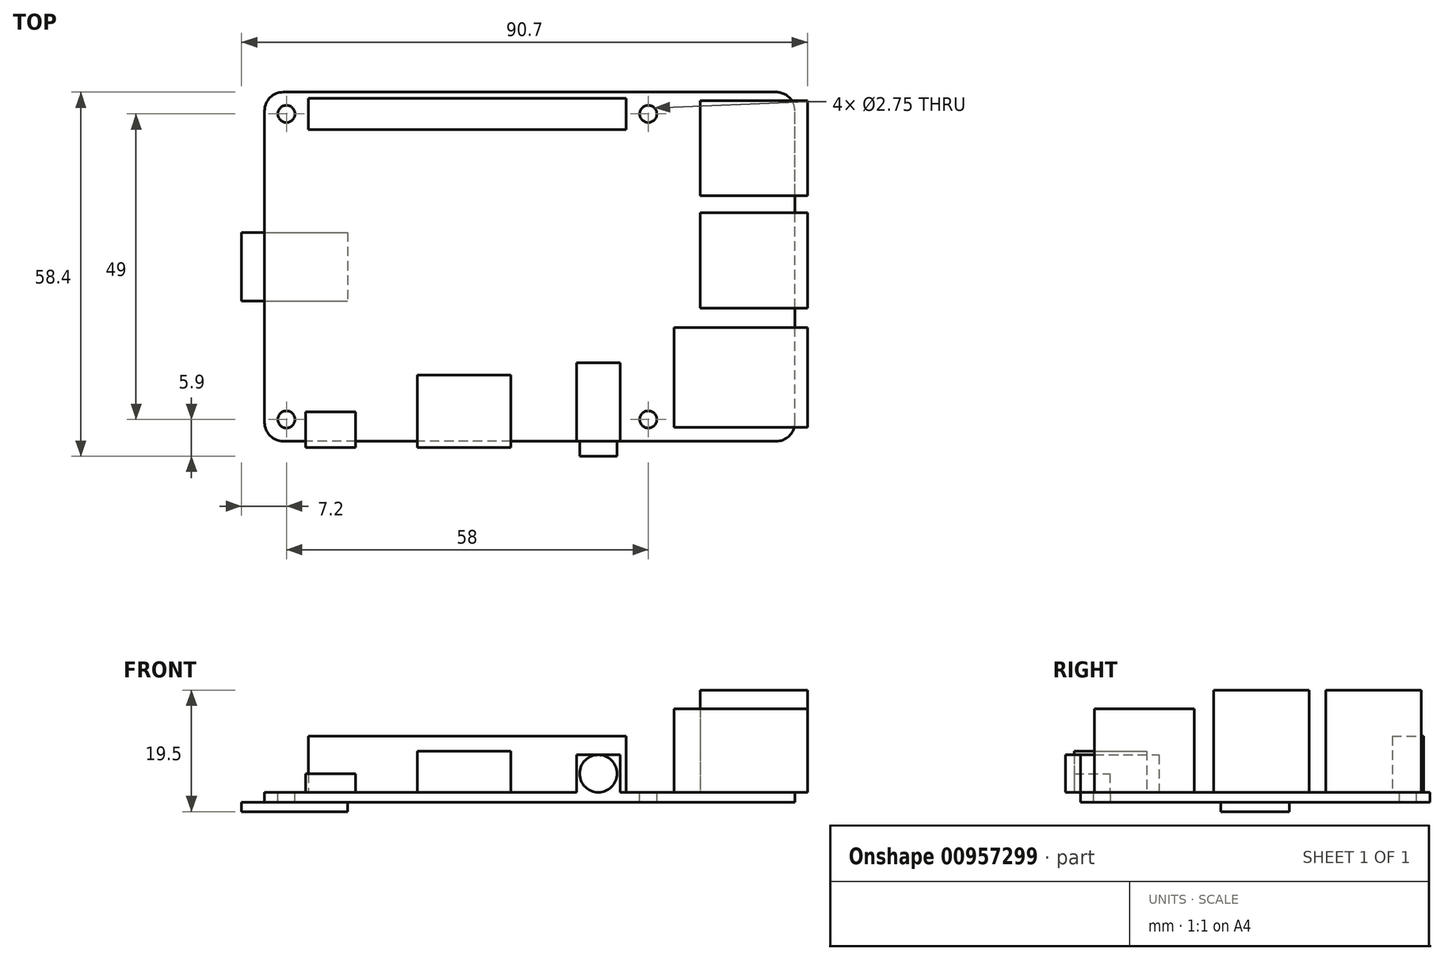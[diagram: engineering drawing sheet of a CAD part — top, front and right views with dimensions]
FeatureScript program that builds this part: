
annotation { "Feature Type Name" : "Feature", "Feature Type Description" : "" }
export const myFeature = defineFeature(function(context is Context, id is Id, definition is map)
    precondition{}
    {
        {
            var Q0;
            Q0=qCreatedBy(makeId("Top.planeOp"),FACE);
            var sketch = newSketch(context, id + "F0", { "sketchPlane" : qUnion([Q0])});
            skLineSegment(sketch, "E0.bottom", {"start": v(42.5, -28) * mm, "end": v(-42.5, -28) * mm});
            skLineSegment(sketch, "E0.top", {"start": v(42.5, 28) * mm, "end": v(-42.5, 28) * mm});
            skLineSegment(sketch, "E0.left", {"start": v(42.5, -28) * mm, "end": v(42.5, 28) * mm});
            skLineSegment(sketch, "E0.right", {"start": v(-42.5, -28) * mm, "end": v(-42.5, 28) * mm});
            skPoint(sketch, "E0.middle", {"position": v(0, 0) * mm});
            skSolve(sketch);
        }
        {
            var Q0;
            Q0=qSketchRegion(id+"F0",true);
            extrude(context, id + "F1", {"entities" : qUnion([Q0]), "depth" : 1.6 * mm, "offsetDistance" : 25 * mm});
        }
        {
            var Q0;
            Q0=makeQuery(id+"F1.opExtrude","CAP_FACE",FACE,{"disambiguationData":[OSD([sQuery(id+"F0.wireOp",EDGE,"E0.bottom"),sQuery(id+"F0.wireOp",EDGE,"E0.top"),sQuery(id+"F0.wireOp",EDGE,"E0.left"),sQuery(id+"F0.wireOp",EDGE,"E0.right")])],"isStart":false});
            var sketch = newSketch(context, id + "F2", { "sketchPlane" : qUnion([Q0])});
            skLineSegment(sketch, "E1.bottom", {"start": v(44.5, -25.75) * mm, "end": v(23.1, -25.75) * mm});
            skLineSegment(sketch, "E1.top", {"start": v(44.5, -9.75) * mm, "end": v(23.1, -9.75) * mm});
            skLineSegment(sketch, "E1.left", {"start": v(44.5, -25.75) * mm, "end": v(44.5, -9.75) * mm});
            skLineSegment(sketch, "E1.right", {"start": v(23.1, -25.75) * mm, "end": v(23.1, -9.75) * mm});
            skPoint(sketch, "E1.middle", {"position": v(33.8, -17.75) * mm});
            skSolve(sketch);
        }
        {
            var Q0;
            Q0=qSketchRegion(id+"F2",true);
            extrude(context, id + "F3", {"entities" : qUnion([Q0]), "operationType" : NewBodyOperationType.ADD, "depth" : 13.4 * mm, "offsetDistance" : 25 * mm});
        }
        {
            var Q0;
            Q0=makeQuery(id+"F1.opExtrude","CAP_FACE",FACE,{"disambiguationData":[OSD([sQuery(id+"F0.wireOp",EDGE,"E0.bottom"),sQuery(id+"F0.wireOp",EDGE,"E0.top"),sQuery(id+"F0.wireOp",EDGE,"E0.left"),sQuery(id+"F0.wireOp",EDGE,"E0.right")])],"isStart":false});
            var sketch = newSketch(context, id + "F4", { "sketchPlane" : qUnion([Q0])});
            skLineSegment(sketch, "E2.bottom", {"start": v(44.5, -6.65) * mm, "end": v(27.3, -6.65) * mm});
            skLineSegment(sketch, "E2.top", {"start": v(44.5, 8.65) * mm, "end": v(27.3, 8.65) * mm});
            skLineSegment(sketch, "E2.left", {"start": v(44.5, -6.65) * mm, "end": v(44.5, 8.65) * mm});
            skLineSegment(sketch, "E2.right", {"start": v(27.3, -6.65) * mm, "end": v(27.3, 8.65) * mm});
            skPoint(sketch, "E2.middle", {"position": v(35.9, 1) * mm});
            skLineSegment(sketch, "E3.bottom", {"start": v(44.5, 11.35) * mm, "end": v(27.3, 11.35) * mm});
            skLineSegment(sketch, "E3.top", {"start": v(44.5, 26.65) * mm, "end": v(27.3, 26.65) * mm});
            skLineSegment(sketch, "E3.left", {"start": v(44.5, 11.35) * mm, "end": v(44.5, 26.65) * mm});
            skLineSegment(sketch, "E3.right", {"start": v(27.3, 11.35) * mm, "end": v(27.3, 26.65) * mm});
            skPoint(sketch, "E3.middle", {"position": v(35.9, 19) * mm});
            skSolve(sketch);
        }
        {
            var Q0;
            Q0=qSketchRegion(id+"F4",true);
            extrude(context, id + "F5", {"entities" : qUnion([Q0]), "operationType" : NewBodyOperationType.ADD, "depth" : 16.4 * mm, "offsetDistance" : 25 * mm});
        }
        {
            var Q0;
            Q0=makeQuery(id+"F1.opExtrude","CAP_FACE",FACE,{"disambiguationData":[OSD([sQuery(id+"F0.wireOp",EDGE,"E0.bottom"),sQuery(id+"F0.wireOp",EDGE,"E0.top"),sQuery(id+"F0.wireOp",EDGE,"E0.left"),sQuery(id+"F0.wireOp",EDGE,"E0.right")])],"isStart":false});
            var sketch = newSketch(context, id + "F6", { "sketchPlane" : qUnion([Q0])});
            skLineSegment(sketch, "E4.bottom", {"start": v(-3, -29) * mm, "end": v(-18, -29) * mm});
            skLineSegment(sketch, "E4.top", {"start": v(-3, -17.4) * mm, "end": v(-18, -17.4) * mm});
            skLineSegment(sketch, "E4.left", {"start": v(-3, -29) * mm, "end": v(-3, -17.4) * mm});
            skLineSegment(sketch, "E4.right", {"start": v(-18, -29) * mm, "end": v(-18, -17.4) * mm});
            skPoint(sketch, "E4.middle", {"position": v(-10.5, -23.2) * mm});
            skSolve(sketch);
        }
        {
            var Q0;
            Q0=qSketchRegion(id+"F6",true);
            extrude(context, id + "F7", {"entities" : qUnion([Q0]), "operationType" : NewBodyOperationType.ADD, "depth" : 6.6 * mm, "offsetDistance" : 25 * mm});
        }
        {
            var Q0;
            Q0=makeQuery(id+"F1.opExtrude","CAP_FACE",FACE,{"disambiguationData":[OSD([sQuery(id+"F0.wireOp",EDGE,"E0.bottom"),sQuery(id+"F0.wireOp",EDGE,"E0.top"),sQuery(id+"F0.wireOp",EDGE,"E0.left"),sQuery(id+"F0.wireOp",EDGE,"E0.right")])],"isStart":false});
            var sketch = newSketch(context, id + "F8", { "sketchPlane" : qUnion([Q0])});
            skLineSegment(sketch, "E5.bottom", {"start": v(14.5, -30.4) * mm, "end": v(7.5, -30.4) * mm});
            skLineSegment(sketch, "E5.top", {"start": v(14.5, -15.4) * mm, "end": v(7.5, -15.4) * mm});
            skLineSegment(sketch, "E5.left", {"start": v(14.5, -30.4) * mm, "end": v(14.5, -15.4) * mm});
            skLineSegment(sketch, "E5.right", {"start": v(7.5, -30.4) * mm, "end": v(7.5, -15.4) * mm});
            skPoint(sketch, "E5.middle", {"position": v(11, -22.9) * mm});
            skSolve(sketch);
        }
        {
            var Q0;
            Q0=qSketchRegion(id+"F8",true);
            extrude(context, id + "F9", {"entities" : qUnion([Q0]), "operationType" : NewBodyOperationType.ADD, "depth" : 6 * mm, "offsetDistance" : 25 * mm});
        }
        {
            var Q0;
            Q0=makeQuery(id+"F1.opExtrude","CAP_FACE",FACE,{"disambiguationData":[OSD([sQuery(id+"F0.wireOp",EDGE,"E0.bottom"),sQuery(id+"F0.wireOp",EDGE,"E0.top"),sQuery(id+"F0.wireOp",EDGE,"E0.left"),sQuery(id+"F0.wireOp",EDGE,"E0.right")])],"isStart":false});
            var sketch = newSketch(context, id + "F10", { "sketchPlane" : qUnion([Q0])});
            skLineSegment(sketch, "E6.bottom", {"start": v(-27.9, -29) * mm, "end": v(-35.9, -29) * mm});
            skLineSegment(sketch, "E6.top", {"start": v(-27.9, -23.3) * mm, "end": v(-35.9, -23.3) * mm});
            skLineSegment(sketch, "E6.left", {"start": v(-27.9, -29) * mm, "end": v(-27.9, -23.3) * mm});
            skLineSegment(sketch, "E6.right", {"start": v(-35.9, -29) * mm, "end": v(-35.9, -23.3) * mm});
            skPoint(sketch, "E6.middle", {"position": v(-31.9, -26.15) * mm});
            skSolve(sketch);
        }
        {
            var Q0;
            Q0=qSketchRegion(id+"F10",true);
            extrude(context, id + "F11", {"entities" : qUnion([Q0]), "operationType" : NewBodyOperationType.ADD, "depth" : 3 * mm, "offsetDistance" : 25 * mm});
        }
        {
            var Q0;
            Q0=makeQuery(id+"F1.opExtrude","CAP_FACE",FACE,{"disambiguationData":[OSD([sQuery(id+"F0.wireOp",EDGE,"E0.bottom"),sQuery(id+"F0.wireOp",EDGE,"E0.top"),sQuery(id+"F0.wireOp",EDGE,"E0.left"),sQuery(id+"F0.wireOp",EDGE,"E0.right")])],"isStart":true});
            var sketch = newSketch(context, id + "F12", { "sketchPlane" : qUnion([Q0])});
            skLineSegment(sketch, "E7.bottom", {"start": v(-46.2, -5.5) * mm, "end": v(-29.2, -5.5) * mm});
            skLineSegment(sketch, "E7.top", {"start": v(-46.2, 5.5) * mm, "end": v(-29.2, 5.5) * mm});
            skLineSegment(sketch, "E7.left", {"start": v(-46.2, -5.5) * mm, "end": v(-46.2, 5.5) * mm});
            skLineSegment(sketch, "E7.right", {"start": v(-29.2, -5.5) * mm, "end": v(-29.2, 5.5) * mm});
            skPoint(sketch, "E7.middle", {"position": v(-37.7, 0) * mm});
            skSolve(sketch);
        }
        {
            var Q0;
            Q0=qSketchRegion(id+"F12",true);
            extrude(context, id + "F13", {"entities" : qUnion([Q0]), "operationType" : NewBodyOperationType.ADD, "depth" : 1.5 * mm, "offsetDistance" : 25 * mm});
        }
        {
            var Q0;
            Q0=makeQuery(id+"F1.opExtrude","CAP_FACE",FACE,{"disambiguationData":[OSD([sQuery(id+"F0.wireOp",EDGE,"E0.bottom"),sQuery(id+"F0.wireOp",EDGE,"E0.top"),sQuery(id+"F0.wireOp",EDGE,"E0.left"),sQuery(id+"F0.wireOp",EDGE,"E0.right")])],"isStart":false});
            var sketch = newSketch(context, id + "F14", { "sketchPlane" : qUnion([Q0])});
            skCircle(sketch, "E8", {"center": v(-39, -24.5) * mm, "radius": 1.38 * mm});
            skCircle(sketch, "E9", {"center": v(19, -24.5) * mm, "radius": 1.38 * mm});
            skCircle(sketch, "E10.MirrorC", {"center": v(-39, 24.5) * mm, "radius": 1.38 * mm});
            skCircle(sketch, "E11.MirrorC", {"center": v(19, 24.5) * mm, "radius": 1.38 * mm});
            skSolve(sketch);
        }
        {
            var Q0;
            Q0=qSketchRegion(id+"F14",true);
            extrude(context, id + "F15", {"entities" : qUnion([Q0]), "operationType" : NewBodyOperationType.REMOVE, "endBound" : BoundingType.THROUGH_ALL, "oppositeDirection" : true, "depth" : 25 * mm, "offsetDistance" : 25 * mm});
        }
        {
            var Q0;
            Q0=makeQuery(id+"F1.opExtrude","SWEPT_EDGE",EDGE,{"disambiguationData":[OSD([sQuery(id+"F0.wireOp",EDGE,"E0.bottom"),sQuery(id+"F0.wireOp",EDGE,"E0.right")])]});
            var Q1;
            Q1=makeQuery(id+"F1.opExtrude","SWEPT_EDGE",EDGE,{"disambiguationData":[OSD([sQuery(id+"F0.wireOp",EDGE,"E0.bottom"),sQuery(id+"F0.wireOp",EDGE,"E0.left")])]});
            var Q2;
            Q2=makeQuery(id+"F1.opExtrude","SWEPT_EDGE",EDGE,{"disambiguationData":[OSD([sQuery(id+"F0.wireOp",EDGE,"E0.top"),sQuery(id+"F0.wireOp",EDGE,"E0.left")])]});
            var Q3;
            Q3=makeQuery(id+"F1.opExtrude","SWEPT_EDGE",EDGE,{"disambiguationData":[OSD([sQuery(id+"F0.wireOp",EDGE,"E0.top"),sQuery(id+"F0.wireOp",EDGE,"E0.right")])]});
            fillet(context, id + "F16", {"entities" : qUnion([Q0, Q1, Q2, Q3]), "radius" : 3 * mm, "tangentPropagation" : true, "allowEdgeOverflow" : false});
        }
        {
            var Q0;
            Q0=makeQuery(id+"F1.opExtrude","CAP_FACE",FACE,{"disambiguationData":[OSD([sQuery(id+"F0.wireOp",EDGE,"E0.bottom"),sQuery(id+"F0.wireOp",EDGE,"E0.top"),sQuery(id+"F0.wireOp",EDGE,"E0.left"),sQuery(id+"F0.wireOp",EDGE,"E0.right")])],"isStart":false});
            var sketch = newSketch(context, id + "F17", { "sketchPlane" : qUnion([Q0])});
            skLineSegment(sketch, "E12.bottom", {"start": v(15.45, 21.98) * mm, "end": v(-35.45, 21.98) * mm});
            skLineSegment(sketch, "E12.top", {"start": v(15.45, 26.98) * mm, "end": v(-35.45, 26.98) * mm});
            skLineSegment(sketch, "E12.left", {"start": v(15.45, 21.98) * mm, "end": v(15.45, 26.98) * mm});
            skLineSegment(sketch, "E12.right", {"start": v(-35.45, 21.98) * mm, "end": v(-35.45, 26.98) * mm});
            skPoint(sketch, "E12.middle", {"position": v(-10, 24.48) * mm});
            skSolve(sketch);
        }
        {
            var Q0;
            Q0=qSketchRegion(id+"F17",true);
            extrude(context, id + "F18", {"entities" : qUnion([Q0]), "operationType" : NewBodyOperationType.ADD, "depth" : 9 * mm, "offsetDistance" : 25 * mm});
        }
        {
            var Q0;
            Q0=makeQuery(id+"F9.opExtrude","SWEPT_FACE",FACE,{"disambiguationData":[OSD([sQuery(id+"F8.wireOp",EDGE,"E5.bottom")])]});
            var sketch = newSketch(context, id + "F19", { "sketchPlane" : qUnion([Q0])});
            skCircle(sketch, "E13", {"center": v(11, 4.6) * mm, "radius": 3 * mm});
            skPoint(sketch, "E13.centerSnap0", {"position": v(11, 7.6) * mm});
            skPoint(sketch, "E13.centerSnap1", {"position": v(7.5, 4.6) * mm});
            skLineSegment(sketch, "E14.bottom", {"start": v(14.5, 1.6) * mm, "end": v(7.5, 1.6) * mm});
            skLineSegment(sketch, "E14.top", {"start": v(14.5, 7.6) * mm, "end": v(7.5, 7.6) * mm});
            skLineSegment(sketch, "E14.left", {"start": v(14.5, 1.6) * mm, "end": v(14.5, 7.6) * mm});
            skLineSegment(sketch, "E14.right", {"start": v(7.5, 1.6) * mm, "end": v(7.5, 7.6) * mm});
            skSolve(sketch);
        }
        {
            var Q0;
            {var subQ5=sQuery(id+"F19.wireOp",EDGE,"E14.left");Q0=makeQuery(id+"F19.imprint","IMPRINT",FACE,{"disambiguationData":[TD([[makeQuery(id+"F19.imprint","IMPRINT",EDGE,{"derivedFrom":subQ5}),-1.0]])]});}
            var Q1;
            {var subQ5=sQuery(id+"F19.wireOp",EDGE,"E14.right");Q1=makeQuery(id+"F19.imprint","IMPRINT",FACE,{"disambiguationData":[TD([[makeQuery(id+"F19.imprint","IMPRINT",EDGE,{"derivedFrom":subQ5}),1.0]])]});}
            extrude(context, id + "F20", {"entities" : qUnion([Q0, Q1]), "operationType" : NewBodyOperationType.REMOVE, "oppositeDirection" : true, "depth" : 2.4 * mm, "offsetDistance" : 25 * mm});
        }
    });
